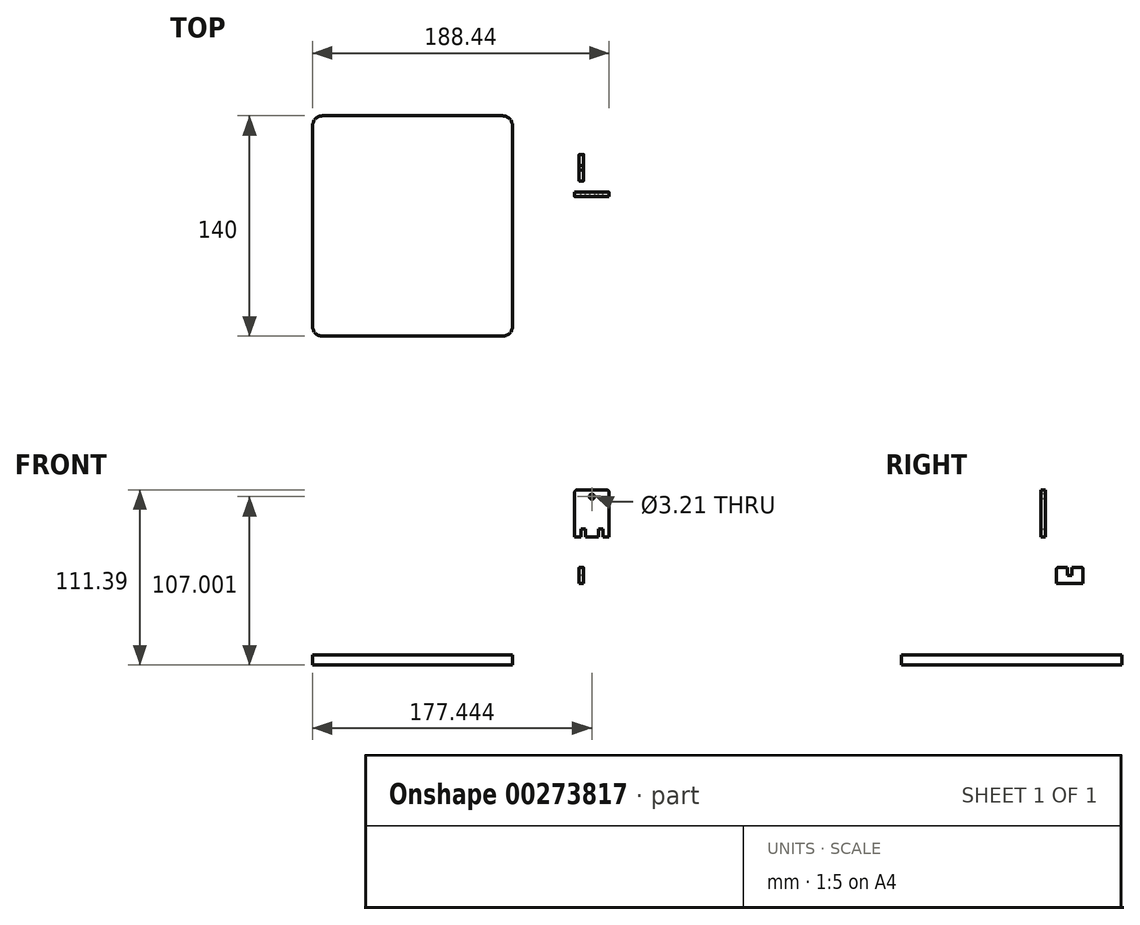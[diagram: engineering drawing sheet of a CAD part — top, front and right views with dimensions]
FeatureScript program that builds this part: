
annotation { "Feature Type Name" : "Feature", "Feature Type Description" : "" }
export const myFeature = defineFeature(function(context is Context, id is Id, definition is map)
    precondition{}
    {
        {
            assignVariable(context, id + "F0", {"name" : "m", "anyValue" : 2.8 * mm});
        }
        {
            var Q0;
            Q0=qCreatedBy(makeId("Top.planeOp"),FACE);
            var sketch = newSketch(context, id + "F1", { "sketchPlane" : qUnion([Q0])});
            skLineSegment(sketch, "E0.bottom", {"start": v(-53.87, 111.57) * mm, "end": v(60.43, 111.57) * mm});
            skLineSegment(sketch, "E0.top", {"start": v(-53.87, -28.43) * mm, "end": v(60.43, -28.43) * mm});
            skLineSegment(sketch, "E0.left", {"start": v(-60.22, 105.22) * mm, "end": v(-60.22, -22.08) * mm});
            skLineSegment(sketch, "E0.right", {"start": v(66.78, 105.22) * mm, "end": v(66.78, -22.08) * mm});
            skPoint(sketch, "E1.visualSharp", {"position": v(-60.22, 111.57) * mm});
            skArc(sketch, "E1.filletArc", {"start": v(-53.87, 111.57) * mm, "mid": v(-58.36, 109.7) * mm, "end": v(-60.22, 105.22) * mm});
            skPoint(sketch, "E2.visualSharp", {"position": v(66.78, 111.57) * mm});
            skArc(sketch, "E2.filletArc", {"start": v(66.78, 105.22) * mm, "mid": v(64.92, 109.7) * mm, "end": v(60.43, 111.57) * mm});
            skPoint(sketch, "E3.visualSharp", {"position": v(66.78, -28.43) * mm});
            skArc(sketch, "E3.filletArc", {"start": v(60.43, -28.43) * mm, "mid": v(64.92, -26.57) * mm, "end": v(66.78, -22.08) * mm});
            skPoint(sketch, "E4.visualSharp", {"position": v(-60.22, -28.43) * mm});
            skArc(sketch, "E4.filletArc", {"start": v(-60.22, -22.08) * mm, "mid": v(-58.36, -26.57) * mm, "end": v(-53.87, -28.43) * mm});
            skSolve(sketch);
        }
        {
            var Q0;
            Q0 = qSketchRegion(id + "F1", true);
            extrude(context, id + "F2", {"entities" : qUnion([Q0]), "depth" : 6.35 * mm});
        }
        {
            var Q0;
            Q0=qCreatedBy(makeId("Front.planeOp"),FACE);
            var sketch = newSketch(context, id + "F3", { "sketchPlane" : qUnion([Q0])});
            skLineSegment(sketch, "E5.bottom", {"start": v(105.32, 44.99) * mm, "end": v(87.13, 44.99) * mm});
            skLineSegment(sketch, "E5.top", {"start": v(107.22, 14.99) * mm, "end": v(103.22, 14.99) * mm});
            skLineSegment(sketch, "E5.left", {"start": v(107.22, 43.08) * mm, "end": v(107.22, 14.99) * mm});
            skLineSegment(sketch, "E5.right", {"start": v(85.22, 43.08) * mm, "end": v(85.22, 14.99) * mm});
            skPoint(sketch, "E6.visualSharp", {"position": v(107.22, 44.99) * mm});
            skArc(sketch, "E6.filletArc", {"start": v(107.22, 43.08) * mm, "mid": v(106.67, 44.43) * mm, "end": v(105.32, 44.99) * mm});
            skPoint(sketch, "E7.visualSharp", {"position": v(85.22, 44.99) * mm});
            skArc(sketch, "E7.filletArc", {"start": v(87.13, 44.99) * mm, "mid": v(85.78, 44.43) * mm, "end": v(85.22, 43.08) * mm});
            skLineSegment(sketch, "E8", {"start": v(103.22, 14.99) * mm, "end": v(103.22, 20.07) * mm});
            skLineSegment(sketch, "E9", {"start": v(103.22, 20.07) * mm, "end": v(100.42, 20.07) * mm});
            skLineSegment(sketch, "E10", {"start": v(100.42, 20.07) * mm, "end": v(100.42, 14.99) * mm});
            skLineSegment(sketch, "E11.trimOffspring", {"start": v(100.42, 14.99) * mm, "end": v(92.02, 14.99) * mm});
            skPoint(sketch, "E12.firstSnap0", {"position": v(101.82, 20.07) * mm});
            skLineSegment(sketch, "E12.bottom", {"start": v(92.02, 20.07) * mm, "end": v(89.22, 20.07) * mm});
            skLineSegment(sketch, "E12.left", {"start": v(92.02, 20.07) * mm, "end": v(92.02, 14.99) * mm});
            skLineSegment(sketch, "E12.right", {"start": v(89.22, 20.07) * mm, "end": v(89.22, 14.99) * mm});
            skLineSegment(sketch, "E13.trimOffspring", {"start": v(89.22, 14.99) * mm, "end": v(85.22, 14.99) * mm});
            skSolve(sketch);
        }
        {
            var Q0;
            Q0=makeQuery(id+"F3.imprint","IMPRINT",FACE,{"disambiguationData":[TD([[makeQuery(id+"F3.imprint","IMPRINT",EDGE,{"derivedFrom":sQuery(id+"F3.wireOp",EDGE,"E5.bottom")}),1.0]])]});
            extrude(context, id + "F4", {"entities" : qUnion([Q0]), "depth" : getVariable(context, 'm')});
        }
        {
            var Q0;
            Q0=qCreatedBy(makeId("Right.planeOp"),FACE);
            var sketch = newSketch(context, id + "F5", { "sketchPlane" : qUnion([Q0])});
            skLineSegment(sketch, "E14.bottom", {"start": v(104.27, -1.4) * mm, "end": v(87.47, -1.4) * mm});
            skLineSegment(sketch, "E14.top", {"start": v(103.27, 8.6) * mm, "end": v(97.27, 8.6) * mm});
            skLineSegment(sketch, "E14.left", {"start": v(104.27, -1.4) * mm, "end": v(104.27, 7.6) * mm});
            skLineSegment(sketch, "E14.right", {"start": v(87.47, -1.4) * mm, "end": v(87.47, 7.6) * mm});
            skPoint(sketch, "E14.middle", {"position": v(95.87, 3.6) * mm});
            skLineSegment(sketch, "E15.top", {"start": v(94.47, 3.6) * mm, "end": v(97.27, 3.6) * mm});
            skLineSegment(sketch, "E15.left", {"start": v(94.47, 8.6) * mm, "end": v(94.47, 3.6) * mm});
            skLineSegment(sketch, "E15.right", {"start": v(97.27, 8.6) * mm, "end": v(97.27, 3.6) * mm});
            skLineSegment(sketch, "E16.trimOffspring", {"start": v(94.47, 8.6) * mm, "end": v(88.47, 8.6) * mm});
            skPoint(sketch, "E17.visualSharp", {"position": v(87.47, 8.6) * mm});
            skArc(sketch, "E17.filletArc", {"start": v(88.47, 8.6) * mm, "mid": v(87.77, 8.3) * mm, "end": v(87.47, 7.6) * mm});
            skPoint(sketch, "E18.visualSharp", {"position": v(104.27, 8.6) * mm});
            skArc(sketch, "E18.filletArc", {"start": v(104.27, 7.6) * mm, "mid": v(103.98, 8.3) * mm, "end": v(103.27, 8.6) * mm});
            skSolve(sketch);
        }
        {
            var Q0;
            Q0=makeQuery(id+"F5.imprint","IMPRINT",FACE,{"disambiguationData":[TD([[makeQuery(id+"F5.imprint","IMPRINT",EDGE,{"derivedFrom":sQuery(id+"F5.wireOp",EDGE,"E14.bottom")}),-1.0]])]});
            extrude(context, id + "F6", {"entities" : qUnion([Q0]), "depth" : getVariable(context, 'm')});
        }
        {
            var Q0;
            Q0=makeQuery(id+"F4.opExtrude","SWEPT_BODY",BODY,{"disambiguationData":[OSD([sQuery(id+"F3.wireOp",EDGE,"E5.bottom"),sQuery(id+"F3.wireOp",EDGE,"E5.top"),sQuery(id+"F3.wireOp",EDGE,"E5.left"),sQuery(id+"F3.wireOp",EDGE,"E5.right"),sQuery(id+"F3.wireOp",EDGE,"E6.filletArc"),sQuery(id+"F3.wireOp",EDGE,"E7.filletArc"),sQuery(id+"F3.wireOp",EDGE,"E8"),sQuery(id+"F3.wireOp",EDGE,"E9"),sQuery(id+"F3.wireOp",EDGE,"E10"),sQuery(id+"F3.wireOp",EDGE,"E11.trimOffspring"),sQuery(id+"F3.wireOp",EDGE,"E12.bottom"),sQuery(id+"F3.wireOp",EDGE,"E12.left"),sQuery(id+"F3.wireOp",EDGE,"E12.right"),sQuery(id+"F3.wireOp",EDGE,"E13.trimOffspring")])]});
            transform(context, id + "F7", {"entities" : qUnion([Q0]), "transformType" : TransformType.TRANSLATION_3D, "dx" : 21 * mm, "dy" : 48.4 * mm, "dz" : 40.2 * mm, "makeCopy" : false});
        }
        {
            var Q0;
            Q0=makeQuery(id+"F6.opExtrude","SWEPT_BODY",BODY,{"disambiguationData":[OSD([sQuery(id+"F5.wireOp",EDGE,"E14.bottom"),sQuery(id+"F5.wireOp",EDGE,"E14.top"),sQuery(id+"F5.wireOp",EDGE,"E14.left"),sQuery(id+"F5.wireOp",EDGE,"E14.right"),sQuery(id+"F5.wireOp",EDGE,"E15.top"),sQuery(id+"F5.wireOp",EDGE,"E15.left"),sQuery(id+"F5.wireOp",EDGE,"E15.right"),sQuery(id+"F5.wireOp",EDGE,"E16.trimOffspring"),sQuery(id+"F5.wireOp",EDGE,"E17.filletArc"),sQuery(id+"F5.wireOp",EDGE,"E18.filletArc")])]});
            transform(context, id + "F8", {"entities" : qUnion([Q0]), "transformType" : TransformType.TRANSLATION_3D, "dx" : 109.1 * mm, "dy" : -17.3 * mm, "dz" : 53.4 * mm, "makeCopy" : false});
        }
        {
            var Q0;
            Q0=makeQuery(id+"F4.opExtrude","SWEPT_BODY",BODY,{"disambiguationData":[OSD([sQuery(id+"F3.wireOp",EDGE,"E5.bottom"),sQuery(id+"F3.wireOp",EDGE,"E5.top"),sQuery(id+"F3.wireOp",EDGE,"E5.left"),sQuery(id+"F3.wireOp",EDGE,"E5.right"),sQuery(id+"F3.wireOp",EDGE,"E6.filletArc"),sQuery(id+"F3.wireOp",EDGE,"E7.filletArc"),sQuery(id+"F3.wireOp",EDGE,"E8"),sQuery(id+"F3.wireOp",EDGE,"E9"),sQuery(id+"F3.wireOp",EDGE,"E10"),sQuery(id+"F3.wireOp",EDGE,"E11.trimOffspring"),sQuery(id+"F3.wireOp",EDGE,"E12.bottom"),sQuery(id+"F3.wireOp",EDGE,"E12.left"),sQuery(id+"F3.wireOp",EDGE,"E12.right"),sQuery(id+"F3.wireOp",EDGE,"E13.trimOffspring")])]});
            transform(context, id + "F9", {"entities" : qUnion([Q0]), "transformType" : TransformType.TRANSLATION_3D, "dx" : 0 * mm, "dy" : 14.6 * mm, "dz" : 26.2 * mm, "makeCopy" : false});
        }
        {
            var Q0;
            Q0=makeQuery(id+"F4.opExtrude","CAP_FACE",FACE,{"disambiguationData":[OSD([sQuery(id+"F3.wireOp",EDGE,"E5.bottom"),sQuery(id+"F3.wireOp",EDGE,"E5.top"),sQuery(id+"F3.wireOp",EDGE,"E5.left"),sQuery(id+"F3.wireOp",EDGE,"E5.right"),sQuery(id+"F3.wireOp",EDGE,"E6.filletArc"),sQuery(id+"F3.wireOp",EDGE,"E7.filletArc"),sQuery(id+"F3.wireOp",EDGE,"E8"),sQuery(id+"F3.wireOp",EDGE,"E9"),sQuery(id+"F3.wireOp",EDGE,"E10"),sQuery(id+"F3.wireOp",EDGE,"E11.trimOffspring"),sQuery(id+"F3.wireOp",EDGE,"E12.bottom"),sQuery(id+"F3.wireOp",EDGE,"E12.left"),sQuery(id+"F3.wireOp",EDGE,"E12.right"),sQuery(id+"F3.wireOp",EDGE,"E13.trimOffspring")])],"isStart":false});
            var sketch = newSketch(context, id + "F10", { "sketchPlane" : qUnion([Q0])});
            skPoint(sketch, "E19", {"position": v(117.22, 81.39) * mm});
            skPoint(sketch, "E20", {"position": v(117.22, 111.39) * mm});
            skPoint(sketch, "E21", {"position": v(117.22, 107) * mm});
            skCircle(sketch, "E22", {"center": v(117.22, 107) * mm, "radius": 1.6 * mm});
            skSolve(sketch);
        }
        {
            var Q0;
            Q0 = qSketchRegion(id + "F10", true);
            extrude(context, id + "F11", {"entities" : qUnion([Q0]), "operationType" : NewBodyOperationType.REMOVE, "endBound" : BoundingType.UP_TO_NEXT, "oppositeDirection" : true, "depth" : 5.8 * mm});
        }
    });
